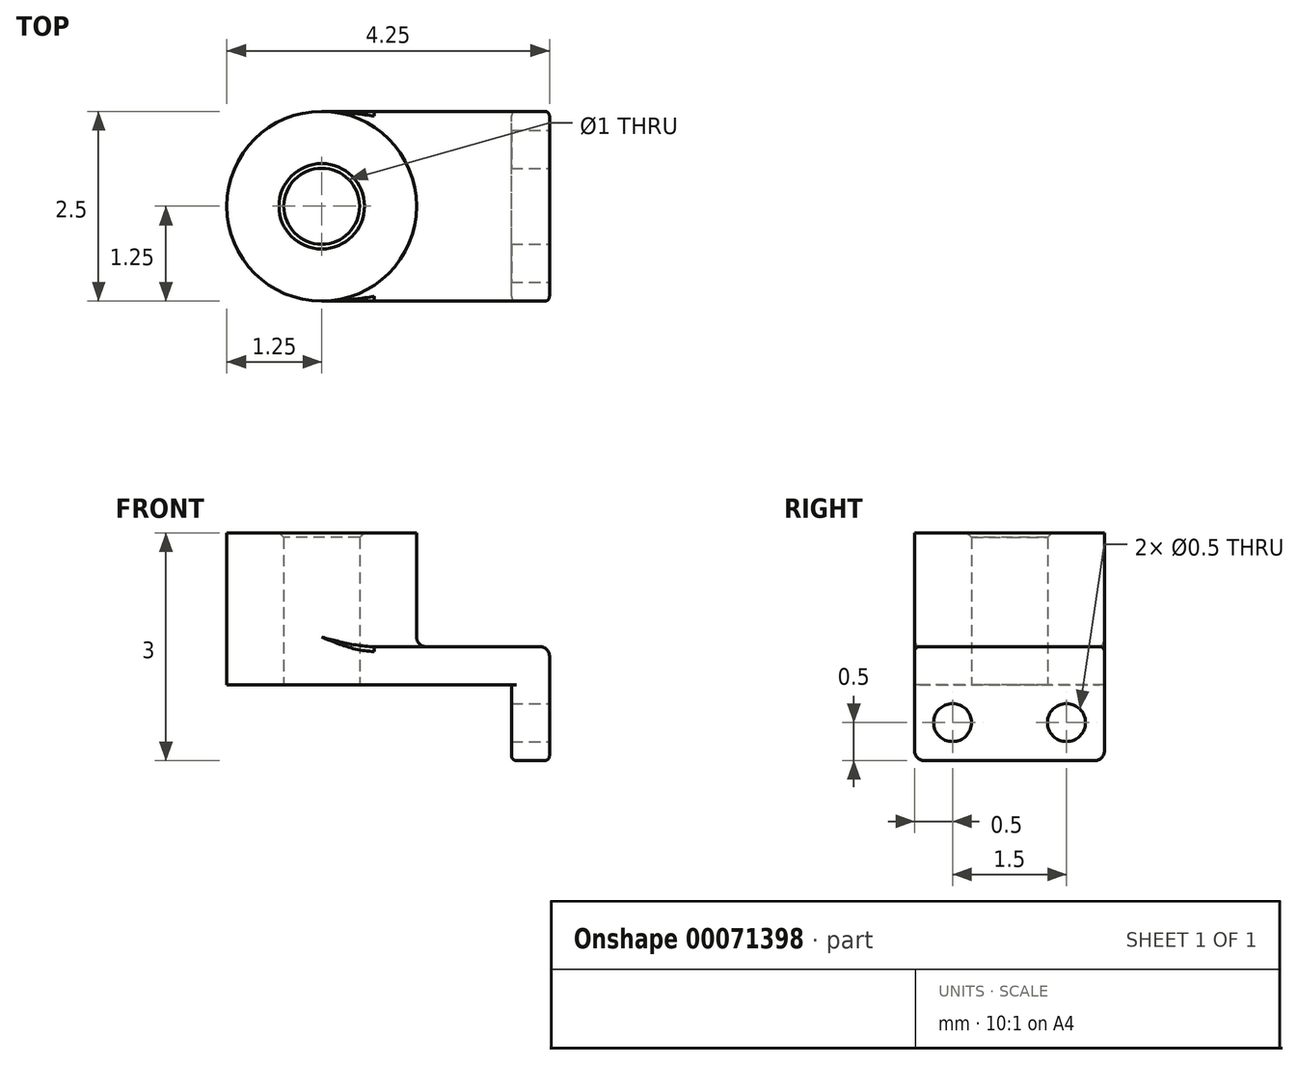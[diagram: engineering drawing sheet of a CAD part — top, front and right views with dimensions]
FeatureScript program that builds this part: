
annotation { "Feature Type Name" : "Feature", "Feature Type Description" : "" }
export const myFeature = defineFeature(function(context is Context, id is Id, definition is map)
    precondition{}
    {
        {
            var Q0;
            Q0=qCreatedBy(makeId("Top.planeOp"),FACE);
            var sketch = newSketch(context, id + "F0", { "sketchPlane" : qUnion([Q0])});
            skLineSegment(sketch, "E0.rect.bottom", {"start": v(1.5, -1.25) * mm, "end": v(-1.5, -1.25) * mm});
            skLineSegment(sketch, "E0.rect.top", {"start": v(1.5, 1.25) * mm, "end": v(-1.5, 1.25) * mm});
            skLineSegment(sketch, "E0.rect.left", {"start": v(1.5, -1.25) * mm, "end": v(1.5, 1.25) * mm});
            skLineSegment(sketch, "E0.rect.right", {"start": v(-1.5, -1.25) * mm, "end": v(-1.5, 1.25) * mm});
            skPoint(sketch, "E0.rect.middle", {"position": v(0, 0) * mm});
            skCircle(sketch, "E1", {"center": v(-1.5, 0) * mm, "radius": 1.25 * mm});
            skCircle(sketch, "E2", {"center": v(-1.5, 0) * mm, "radius": 0.5 * mm});
            skSolve(sketch);
        }
        {
            var Q0;
            {var subQ0=sQuery(id+"F0.wireOp",EDGE,"E0.rect.bottom");Q0=makeQuery(id+"F0.imprint","IMPRINT",FACE,{"disambiguationData":[TD([[makeQuery(id+"F0.imprint","IMPRINT",EDGE,{"derivedFrom":subQ0}),-1.0]])]});}
            var Q1;
            {var subQ1=sQuery(id+"F0.wireOp",EDGE,"E0.rect.right");var subQ3=sQuery(id+"F0.wireOp",EDGE,"E2");var subQ4=makeQuery(id+"F0.imprint","INTERSECT",VERTEX,{"disambiguationData":[OD(0.0)],"derivedFrom":[subQ1,subQ3]});Q1=makeQuery(id+"F0.imprint","IMPRINT",FACE,{"disambiguationData":[TD([[makeQuery(id+"F0.imprint","IMPRINT",EDGE,{"disambiguationData":[TD([[subQ4,-1.0]])],"derivedFrom":subQ3}),-1.0]])]});}
            var Q2;
            {var subQ1=sQuery(id+"F0.wireOp",EDGE,"E0.rect.right");var subQ3=sQuery(id+"F0.wireOp",EDGE,"E2");var subQ4=makeQuery(id+"F0.imprint","INTERSECT",VERTEX,{"disambiguationData":[OD(0.0)],"derivedFrom":[subQ1,subQ3]});Q2=makeQuery(id+"F0.imprint","IMPRINT",FACE,{"disambiguationData":[TD([[makeQuery(id+"F0.imprint","IMPRINT",EDGE,{"disambiguationData":[TD([[subQ4,1.0]])],"derivedFrom":subQ3}),-1.0]])]});}
            extrude(context, id + "F1", {"entities" : qUnion([Q0, Q1, Q2]), "depth" : .5 * mm});
        }
        {
            var Q0;
            {var subQ1=sQuery(id+"F0.wireOp",EDGE,"E0.rect.right");var subQ3=sQuery(id+"F0.wireOp",EDGE,"E2");var subQ4=makeQuery(id+"F0.imprint","INTERSECT",VERTEX,{"disambiguationData":[OD(0.0)],"derivedFrom":[subQ1,subQ3]});Q0=makeQuery(id+"F0.imprint","IMPRINT",FACE,{"disambiguationData":[TD([[makeQuery(id+"F0.imprint","IMPRINT",EDGE,{"disambiguationData":[TD([[subQ4,-1.0]])],"derivedFrom":subQ3}),-1.0]])]});}
            var Q1;
            {var subQ1=sQuery(id+"F0.wireOp",EDGE,"E0.rect.right");var subQ3=sQuery(id+"F0.wireOp",EDGE,"E2");var subQ4=makeQuery(id+"F0.imprint","INTERSECT",VERTEX,{"disambiguationData":[OD(0.0)],"derivedFrom":[subQ1,subQ3]});Q1=makeQuery(id+"F0.imprint","IMPRINT",FACE,{"disambiguationData":[TD([[makeQuery(id+"F0.imprint","IMPRINT",EDGE,{"disambiguationData":[TD([[subQ4,1.0]])],"derivedFrom":subQ3}),-1.0]])]});}
            extrude(context, id + "F2", {"entities" : qUnion([Q0, Q1]), "operationType" : NewBodyOperationType.ADD, "depth" : 2 * mm});
        }
        {
            var Q0;
            Q0=makeQuery(id+"F1.opExtrude","SWEPT_FACE",FACE,{"disambiguationData":[OSD([sQuery(id+"F0.wireOp",EDGE,"E0.rect.left")])]});
            var sketch = newSketch(context, id + "F3", { "sketchPlane" : qUnion([Q0])});
            skLineSegment(sketch, "E3.bottom", {"start": v(-1.25, 0.5) * mm, "end": v(1.25, 0.5) * mm});
            skLineSegment(sketch, "E3.top", {"start": v(-1.25, -1) * mm, "end": v(1.25, -1) * mm});
            skLineSegment(sketch, "E3.left", {"start": v(-1.25, 0.5) * mm, "end": v(-1.25, -1) * mm});
            skLineSegment(sketch, "E3.right", {"start": v(1.25, 0.5) * mm, "end": v(1.25, -1) * mm});
            skLineSegment(sketch, "E4", {"start": v(0, 0.5) * mm, "end": v(0, -1) * mm, "construction": true});
            skCircle(sketch, "E5", {"center": v(-0.75, -0.5) * mm, "radius": 0.25 * mm});
            skCircle(sketch, "E6.MirrorC", {"center": v(0.75, -0.5) * mm, "radius": 0.25 * mm});
            skSolve(sketch);
        }
        {
            var Q0;
            Q0 = qSketchRegion(id + "F3", true);
            extrude(context, id + "F4", {"entities" : qUnion([Q0]), "operationType" : NewBodyOperationType.ADD, "oppositeDirection" : true, "depth" : .5 * mm});
        }
        {
            var Q0;
            {var subQ0=sQuery(id+"F0.wireOp",EDGE,"E1");Q0=makeQuery(id+"F2.boolean.opBoolean","INTERSECT",EDGE,{"derivedFrom":[makeQuery(id+"F1.opExtrude","CAP_FACE",FACE,{"disambiguationData":[OSD([sQuery(id+"F0.wireOp",EDGE,"E0.rect.bottom"),sQuery(id+"F0.wireOp",EDGE,"E0.rect.top"),sQuery(id+"F0.wireOp",EDGE,"E0.rect.left"),subQ0,sQuery(id+"F0.wireOp",EDGE,"E2")])],"isStart":false}),makeQuery(id+"F2.opExtrude","SWEPT_FACE",FACE,{"disambiguationData":[OSD([subQ0])]})]});}
            var Q1;
            Q1=makeQuery(id+"F1.opExtrude","CAP_EDGE",EDGE,{"disambiguationData":[OSD([sQuery(id+"F0.wireOp",EDGE,"E0.rect.left")])],"isStart":false});
            var Q2;
            Q2=makeQuery(id+"F4.opExtrude","SWEPT_EDGE",EDGE,{"disambiguationData":[OSD([sQuery(id+"F3.wireOp",EDGE,"E3.top"),sQuery(id+"F3.wireOp",EDGE,"E3.right")])]});
            var Q3;
            Q3=makeQuery(id+"F4.opExtrude","SWEPT_EDGE",EDGE,{"disambiguationData":[OSD([sQuery(id+"F3.wireOp",EDGE,"E3.top"),sQuery(id+"F3.wireOp",EDGE,"E3.left")])]});
            fillet(context, id + "F5", {"entities" : qUnion([Q0, Q1, Q2, Q3]), "radius" : (1 / 8) * mm, "tangentPropagation" : true, "allowEdgeOverflow" : false});
        }
        {
            var Q0;
            Q0=makeQuery(id+"F4.opExtrude","CAP_EDGE",EDGE,{"disambiguationData":[OSD([sQuery(id+"F3.wireOp",EDGE,"E3.left")])],"isStart":false});
            var Q1;
            Q1=makeQuery(id+"F4.boolean.opBoolean","MERGE",EDGE,{"derivedFrom":[makeQuery(id+"F1.opExtrude","SWEPT_EDGE",EDGE,{"disambiguationData":[OSD([sQuery(id+"F0.wireOp",EDGE,"E0.rect.bottom"),sQuery(id+"F0.wireOp",EDGE,"E0.rect.left")])]}),makeQuery(id+"F4.opExtrude","CAP_EDGE",EDGE,{"disambiguationData":[OSD([sQuery(id+"F3.wireOp",EDGE,"E3.left")])],"isStart":true})]});
            var Q2;
            Q2=makeQuery(id+"F4.boolean.opBoolean","MERGE",EDGE,{"derivedFrom":[makeQuery(id+"F1.opExtrude","SWEPT_EDGE",EDGE,{"disambiguationData":[OSD([sQuery(id+"F0.wireOp",EDGE,"E0.rect.top"),sQuery(id+"F0.wireOp",EDGE,"E0.rect.left")])]}),makeQuery(id+"F4.opExtrude","CAP_EDGE",EDGE,{"disambiguationData":[OSD([sQuery(id+"F3.wireOp",EDGE,"E3.right")])],"isStart":true})]});
            var Q3;
            Q3=makeQuery(id+"F4.opExtrude","CAP_EDGE",EDGE,{"disambiguationData":[OSD([sQuery(id+"F3.wireOp",EDGE,"E3.right")])],"isStart":false});
            var Q4;
            Q4=makeQuery(id+"F1.opExtrude","CAP_EDGE",EDGE,{"disambiguationData":[OSD([sQuery(id+"F0.wireOp",EDGE,"E0.rect.top")])],"isStart":false});
            var Q5;
            Q5=makeQuery(id+"F1.opExtrude","CAP_EDGE",EDGE,{"disambiguationData":[OSD([sQuery(id+"F0.wireOp",EDGE,"E0.rect.bottom")])],"isStart":false});
            fillet(context, id + "F6", {"entities" : qUnion([Q0, Q1, Q2, Q3, Q4, Q5]), "radius" : (1 / 16) * mm, "tangentPropagation" : true, "allowEdgeOverflow" : false});
        }
        {
            var Q0;
            Q0=makeQuery(id+"F2.opExtrude","CAP_EDGE",EDGE,{"disambiguationData":[OSD([sQuery(id+"F0.wireOp",EDGE,"E2")])],"isStart":false});
            chamfer(context, id + "F7", {"entities" : qUnion([Q0]), "width" : (1 / 16) * mm, "tangentPropagation" : true});
        }
    });
